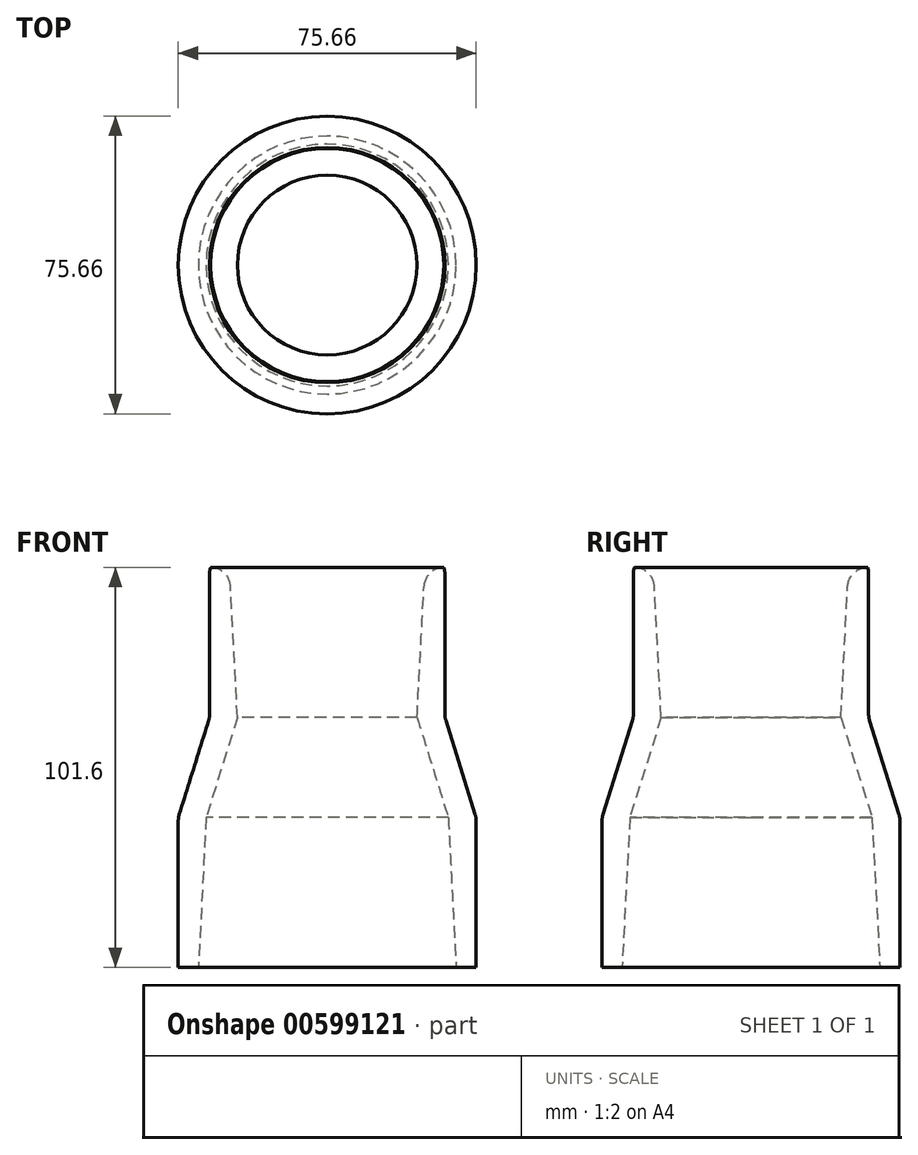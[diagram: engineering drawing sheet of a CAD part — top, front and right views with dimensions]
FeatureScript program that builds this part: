
annotation { "Feature Type Name" : "Feature", "Feature Type Description" : "" }
export const myFeature = defineFeature(function(context is Context, id is Id, definition is map)
    precondition{}
    {
        {
            var Q0;
            Q0=qCreatedBy(makeId("Front.planeOp"),FACE);
            var sketch = newSketch(context, id + "F0", { "sketchPlane" : qUnion([Q0])});
            skLineSegment(sketch, "E0", {"start": v(0, 63.5) * mm, "end": v(0, -63.5) * mm, "construction": true});
            skLineSegment(sketch, "E1", {"start": v(-63.5, 0) * mm, "end": v(63.5, 0) * mm, "construction": true});
            skLineSegment(sketch, "E2", {"start": v(24.81, 50.8) * mm, "end": v(29.9, 50.8) * mm});
            skLineSegment(sketch, "E3", {"start": v(29.9, 50.8) * mm, "end": v(29.9, 12.7) * mm});
            skLineSegment(sketch, "E4", {"start": v(29.9, 12.7) * mm, "end": v(22.81, 12.7) * mm});
            skLineSegment(sketch, "E5", {"start": v(22.81, 12.7) * mm, "end": v(24.81, 50.8) * mm});
            skLineSegment(sketch, "E6", {"start": v(30.75, -12.7) * mm, "end": v(37.83, -12.7) * mm});
            skLineSegment(sketch, "E7", {"start": v(37.83, -12.7) * mm, "end": v(37.83, -50.8) * mm});
            skLineSegment(sketch, "E8", {"start": v(37.83, -50.8) * mm, "end": v(32.75, -50.8) * mm});
            skLineSegment(sketch, "E9", {"start": v(32.75, -50.8) * mm, "end": v(30.75, -12.7) * mm});
            skLineSegment(sketch, "E10", {"start": v(23.81, 31.75) * mm, "end": v(29.9, 31.75) * mm, "construction": true});
            skLineSegment(sketch, "E11", {"start": v(31.75, -31.75) * mm, "end": v(37.83, -31.75) * mm, "construction": true});
            skLineSegment(sketch, "E12", {"start": v(22.81, 12.7) * mm, "end": v(30.75, -12.7) * mm});
            skLineSegment(sketch, "E13", {"start": v(29.9, 12.7) * mm, "end": v(37.83, -12.7) * mm});
            skSolve(sketch);
        }
        {
            var Q0;
            Q0=makeQuery(id+"F0.imprint","IMPRINT",FACE,{"disambiguationData":[TD([[makeQuery(id+"F0.imprint","IMPRINT",EDGE,{"derivedFrom":sQuery(id+"F0.wireOp",EDGE,"E2")}),-1.0]])]});
            var Q1;
            Q1=makeQuery(id+"F0.imprint","IMPRINT",FACE,{"disambiguationData":[TD([[makeQuery(id+"F0.imprint","IMPRINT",EDGE,{"derivedFrom":sQuery(id+"F0.wireOp",EDGE,"E4")}),1.0]])]});
            var Q2;
            Q2=makeQuery(id+"F0.imprint","IMPRINT",FACE,{"disambiguationData":[TD([[makeQuery(id+"F0.imprint","IMPRINT",EDGE,{"derivedFrom":sQuery(id+"F0.wireOp",EDGE,"E6")}),-1.0]])]});
            var Q3;
            Q3=sQuery(id+"F0.wireOp",EDGE,"E0");
            revolve(context, id + "F1", {"entities" : qUnion([Q0, Q1, Q2]), "axis" : qUnion([Q3]), "revolveType" : RevolveType.FULL});
        }
        {
            var Q0;
            Q0=makeQuery(id+"F1.opRevolve","SWEPT_EDGE",EDGE,{"disambiguationData":[OSD([sQuery(id+"F0.wireOp",EDGE,"E2"),sQuery(id+"F0.wireOp",EDGE,"E5")])]});
            fillet(context, id + "F2", {"entities" : qUnion([Q0]), "radius" : 5.08 * mm, "tangentPropagation" : true, "allowEdgeOverflow" : false});
        }
        {
            var Q0;
            Q0=makeQuery(id+"F1.opRevolve","SWEPT_EDGE",EDGE,{"disambiguationData":[OSD([sQuery(id+"F0.wireOp",EDGE,"E6"),sQuery(id+"F0.wireOp",EDGE,"E7"),sQuery(id+"F0.wireOp",EDGE,"E13")])]});
            var Q1;
            Q1=makeQuery(id+"F1.opRevolve","SWEPT_FACE",FACE,{"disambiguationData":[OSD([sQuery(id+"F0.wireOp",EDGE,"E13")])]});
            var Q2;
            Q2=makeQuery(id+"F1.opRevolve","SWEPT_EDGE",EDGE,{"disambiguationData":[OSD([sQuery(id+"F0.wireOp",EDGE,"E2"),sQuery(id+"F0.wireOp",EDGE,"E3")])]});
            fillet(context, id + "F3", {"entities" : qUnion([Q0, Q1, Q2]), "radius" : 5.08 * mm, "allowEdgeOverflow" : false});
        }
    });
